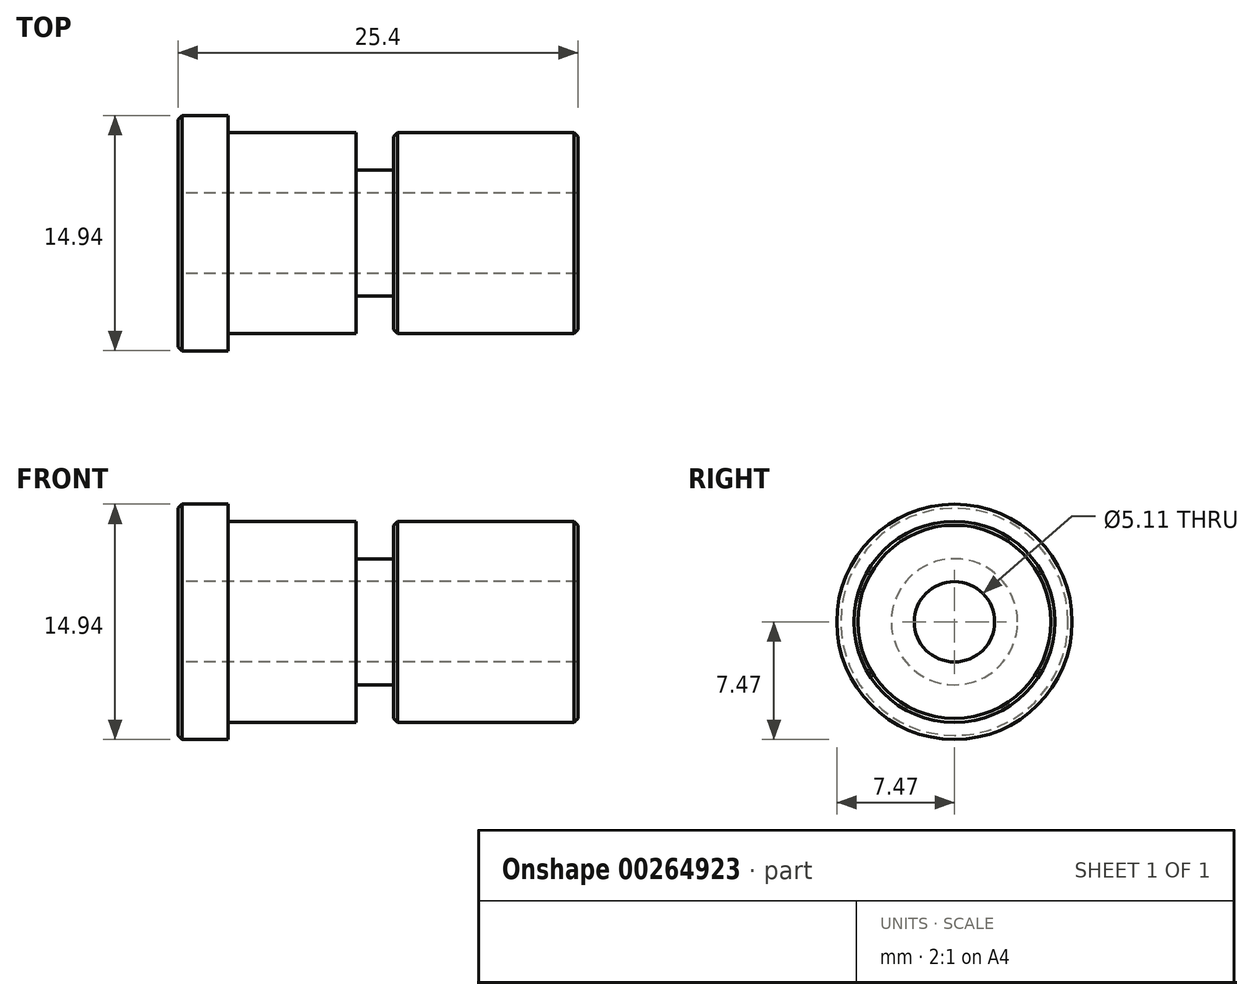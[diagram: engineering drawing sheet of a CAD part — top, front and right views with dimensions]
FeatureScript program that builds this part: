
annotation { "Feature Type Name" : "Feature", "Feature Type Description" : "" }
export const myFeature = defineFeature(function(context is Context, id is Id, definition is map)
    precondition{}
    {
        {
            var Q0;
            Q0=qCreatedBy(makeId("Front.planeOp"),FACE);
            var sketch = newSketch(context, id + "F0", { "sketchPlane" : qUnion([Q0])});
            skLineSegment(sketch, "E0.bottom", {"start": v(3.18, 6.39) * mm, "end": v(11.3, 6.39) * mm});
            skLineSegment(sketch, "E0.top", {"start": v(0, 0) * mm, "end": v(22.86, 0) * mm});
            skLineSegment(sketch, "E1.bottom", {"start": v(0, 7.47) * mm, "end": v(3.18, 7.47) * mm});
            skLineSegment(sketch, "E1.right", {"start": v(3.18, 7.47) * mm, "end": v(3.18, 6.39) * mm});
            skLineSegment(sketch, "E2.top", {"start": v(11.3, 4) * mm, "end": v(13.68, 4) * mm});
            skLineSegment(sketch, "E2.left", {"start": v(11.3, 6.39) * mm, "end": v(11.3, 4) * mm});
            skLineSegment(sketch, "E2.right", {"start": v(13.68, 6.39) * mm, "end": v(13.68, 4) * mm});
            skLineSegment(sketch, "E3.trimOffspring", {"start": v(13.68, 6.39) * mm, "end": v(25.4, 6.39) * mm});
            skLineSegment(sketch, "E4", {"start": v(0, 7.47) * mm, "end": v(0, 0) * mm});
            skPoint(sketch, "E5.orphan", {"position": v(25.4, 0) * mm});
            skLineSegment(sketch, "E6", {"start": v(25.4, 6.39) * mm, "end": v(25.4, 0) * mm});
            skLineSegment(sketch, "E7", {"start": v(22.86, 0) * mm, "end": v(25.4, 0) * mm});
            skSolve(sketch);
        }
        {
            var Q0;
            Q0=makeQuery(id+"F0.imprint","IMPRINT",FACE,{"disambiguationData":[TD([[makeQuery(id+"F0.imprint","IMPRINT",EDGE,{"derivedFrom":sQuery(id+"F0.wireOp",EDGE,"E0.bottom")}),-1.0]])]});
            var Q1;
            Q1=sQuery(id+"F0.wireOp",EDGE,"E0.top");
            revolve(context, id + "F1", {"entities" : qUnion([Q0]), "axis" : qUnion([Q1]), "revolveType" : RevolveType.FULL});
        }
        {
            var Q0;
            Q0=makeQuery(id+"F1.opRevolve","SWEPT_EDGE",EDGE,{"disambiguationData":[OSD([sQuery(id+"F0.wireOp",EDGE,"E1.bottom"),sQuery(id+"F0.wireOp",EDGE,"E4")])]});
            var Q1;
            Q1=makeQuery(id+"F1.opRevolve","SWEPT_EDGE",EDGE,{"disambiguationData":[OSD([sQuery(id+"F0.wireOp",EDGE,"E3.trimOffspring"),sQuery(id+"F0.wireOp",EDGE,"dotk9qRx-SD2O-wkkc-857C-Q5aMrpl4MdWV")])]});
            chamfer(context, id + "F2", {"entities" : qUnion([Q0, Q1]), "width" : 0.25 * mm, "tangentPropagation" : true});
        }
        {
            var Q0;
            Q0=makeQuery(id+"F1.opRevolve","SWEPT_FACE",FACE,{"disambiguationData":[OSD([sQuery(id+"F0.wireOp",EDGE,"E6")])]});
            var sketch = newSketch(context, id + "F3", { "sketchPlane" : qUnion([Q0])});
            skPoint(sketch, "E8", {"position": v(0, 0) * mm});
            skSolve(sketch);
        }
        {
            var Q0;
            Q0=sQuery(id+"F3.wireOp",VERTEX,"E8");
            var Q1;
            Q1=makeQuery(id+"F1.opRevolve","SWEPT_BODY",BODY,{"disambiguationData":[OSD([sQuery(id+"F0.wireOp",EDGE,"E0.bottom"),sQuery(id+"F0.wireOp",EDGE,"E0.top"),sQuery(id+"F0.wireOp",EDGE,"E1.bottom"),sQuery(id+"F0.wireOp",EDGE,"E1.right"),sQuery(id+"F0.wireOp",EDGE,"E2.top"),sQuery(id+"F0.wireOp",EDGE,"E2.left"),sQuery(id+"F0.wireOp",EDGE,"E2.right"),sQuery(id+"F0.wireOp",EDGE,"E3.trimOffspring"),sQuery(id+"F0.wireOp",EDGE,"E4"),sQuery(id+"F0.wireOp",EDGE,"E6"),sQuery(id+"F0.wireOp",EDGE,"E7")])]});
            hole(context, id + "F4", {"style" : HoleStyle.SIMPLE, "endStyle" : HoleEndStyle.THROUGH, "standardTappedOrClearance" : lookupTablePath({ "standard" : "ANSI", "engagement" : "75%", "pitch" : "20 tpi", "size" : "1/4", "type" : "Tapped" }), "standardBlindInLast" : lookupTablePath({ "standard" : "ANSI", "engagement" : "75%", "pitch" : "20 tpi", "size" : "1/4", "type" : "Tapped" }), "holeDiameter" : 5.1 * mm, "showTappedDepth" : true, "tappedDepth" : 25.4 * mm, "tapClearance" : 3, "locations" : qUnion([Q0]), "scope" : qUnion([Q1]), "majorDiameter" : 6.35 * mm, "startStyle" : HoleStartStyle.SKETCH});
        }
    });
